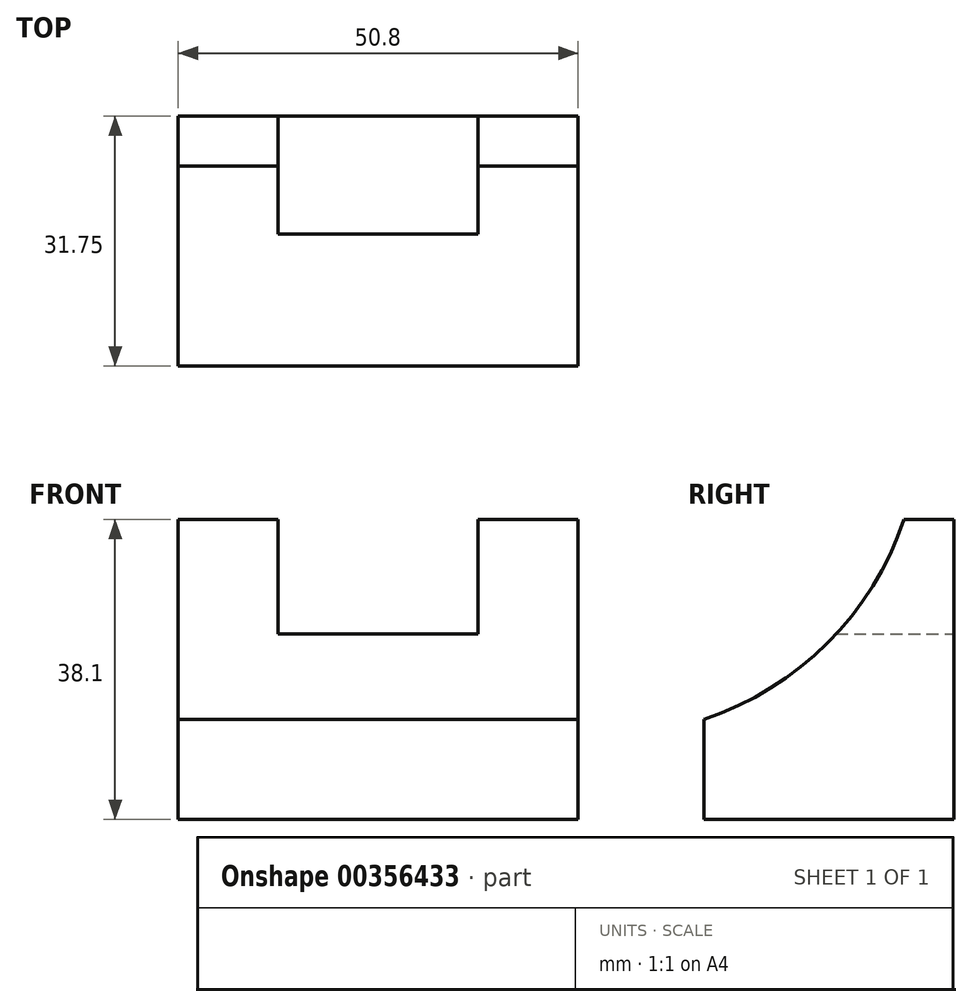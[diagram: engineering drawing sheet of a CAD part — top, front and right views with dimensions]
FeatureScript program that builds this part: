
annotation { "Feature Type Name" : "Feature", "Feature Type Description" : "" }
export const myFeature = defineFeature(function(context is Context, id is Id, definition is map)
    precondition{}
    {
        {
            var Q0;
            Q0=qCreatedBy(makeId("Front.planeOp"),FACE);
            var sketch = newSketch(context, id + "F0", { "sketchPlane" : qUnion([Q0])});
            skLineSegment(sketch, "E0", {"start": v(0, 38.1) * mm, "end": v(0, 0) * mm});
            skLineSegment(sketch, "E1", {"start": v(0, 0) * mm, "end": v(50.8, 0) * mm});
            skLineSegment(sketch, "E2", {"start": v(50.8, 0) * mm, "end": v(50.8, 38.1) * mm});
            skLineSegment(sketch, "E3", {"start": v(50.8, 38.1) * mm, "end": v(0, 38.1) * mm});
            skSolve(sketch);
        }
        {
            var Q0;
            Q0 = qSketchRegion(id + "F0", true);
            extrude(context, id + "F1", {"entities" : qUnion([Q0]), "depth" : 31.75 * mm});
        }
        {
            var Q0;
            Q0=makeQuery(id+"F1.opExtrude","SWEPT_FACE",FACE,{"disambiguationData":[OSD([sQuery(id+"F0.wireOp",EDGE,"E2")])]});
            var sketch = newSketch(context, id + "F2", { "sketchPlane" : qUnion([Q0])});
            skArc(sketch, "E4", {"start": v(-31.75, 12.7) * mm, "mid": v(-16.06, 22.41) * mm, "end": v(-6.35, 38.1) * mm});
            skSolve(sketch);
        }
        {
            var Q0;
            Q0 = qSketchRegion(id + "F2", true);
            var Q1;
            {var subQ0=sQuery(id+"F2.wireOp",EDGE,"E4");Q1=makeQuery(id+"F2.imprint","IMPRINT",FACE,{"disambiguationData":[TD([[makeQuery(id+"F2.imprint","IMPRINT",EDGE,{"derivedFrom":subQ0}),1.0]])]});}
            extrude(context, id + "F3", {"entities" : qUnion([Q0, Q1]), "operationType" : NewBodyOperationType.REMOVE, "oppositeDirection" : true, "depth" : 50.8 * mm});
        }
        {
            var Q0;
            Q0=makeQuery(id+"F1.opExtrude","CAP_FACE",FACE,{"disambiguationData":[OSD([sQuery(id+"F0.wireOp",EDGE,"E0"),sQuery(id+"F0.wireOp",EDGE,"E1"),sQuery(id+"F0.wireOp",EDGE,"E2"),sQuery(id+"F0.wireOp",EDGE,"E3")])],"isStart":true});
            var sketch = newSketch(context, id + "F4", { "sketchPlane" : qUnion([Q0])});
            skLineSegment(sketch, "E5", {"start": v(-38.1, 38.1) * mm, "end": v(-38.1, 23.53) * mm});
            skLineSegment(sketch, "E6", {"start": v(-38.1, 23.53) * mm, "end": v(-12.7, 23.53) * mm});
            skLineSegment(sketch, "E7", {"start": v(-12.7, 23.53) * mm, "end": v(-12.7, 38.1) * mm});
            skSolve(sketch);
        }
        {
            var Q0;
            Q0 = qSketchRegion(id + "F4", true);
            var Q1;
            {var subQ0=sQuery(id+"F4.wireOp",EDGE,"E5");Q1=makeQuery(id+"F4.imprint","IMPRINT",FACE,{"disambiguationData":[TD([[makeQuery(id+"F4.imprint","IMPRINT",EDGE,{"derivedFrom":subQ0}),1.0]])]});}
            extrude(context, id + "F5", {"entities" : qUnion([Q0, Q1]), "operationType" : NewBodyOperationType.REMOVE, "oppositeDirection" : true, "depth" : 25.4 * mm});
        }
    });
